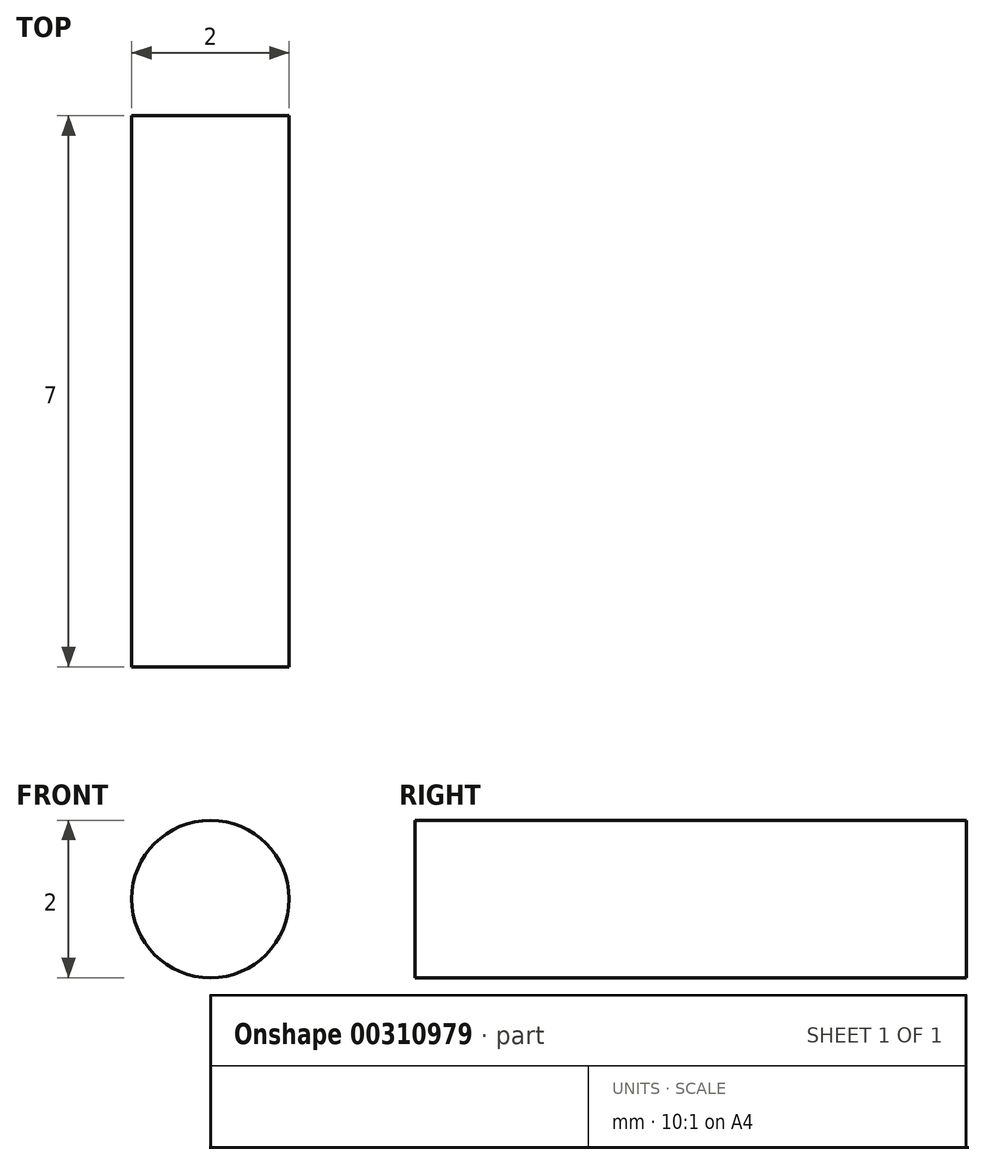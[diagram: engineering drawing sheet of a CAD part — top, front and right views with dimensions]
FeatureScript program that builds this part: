
annotation { "Feature Type Name" : "Feature", "Feature Type Description" : "" }
export const myFeature = defineFeature(function(context is Context, id is Id, definition is map)
    precondition{}
    {
        {
            var Q0;
            Q0=qCreatedBy(makeId("Front.planeOp"),FACE);
            var sketch = newSketch(context, id + "F0", { "sketchPlane" : qUnion([Q0])});
            skCircle(sketch, "E0", {"center": v(0, 0) * mm, "radius": 1 * mm});
            skSolve(sketch);
        }
        {
            var Q0;
            Q0=makeQuery(id+"F0.imprint","IMPRINT",FACE,{"disambiguationData":[TD([[makeQuery(id+"F0.imprint","IMPRINT",EDGE,{"derivedFrom":sQuery(id+"F0.wireOp",EDGE,"E0")}),1.0]])]});
            extrude(context, id + "F1", {"entities" : qUnion([Q0]), "depth" : 7 * mm});
        }
    });
